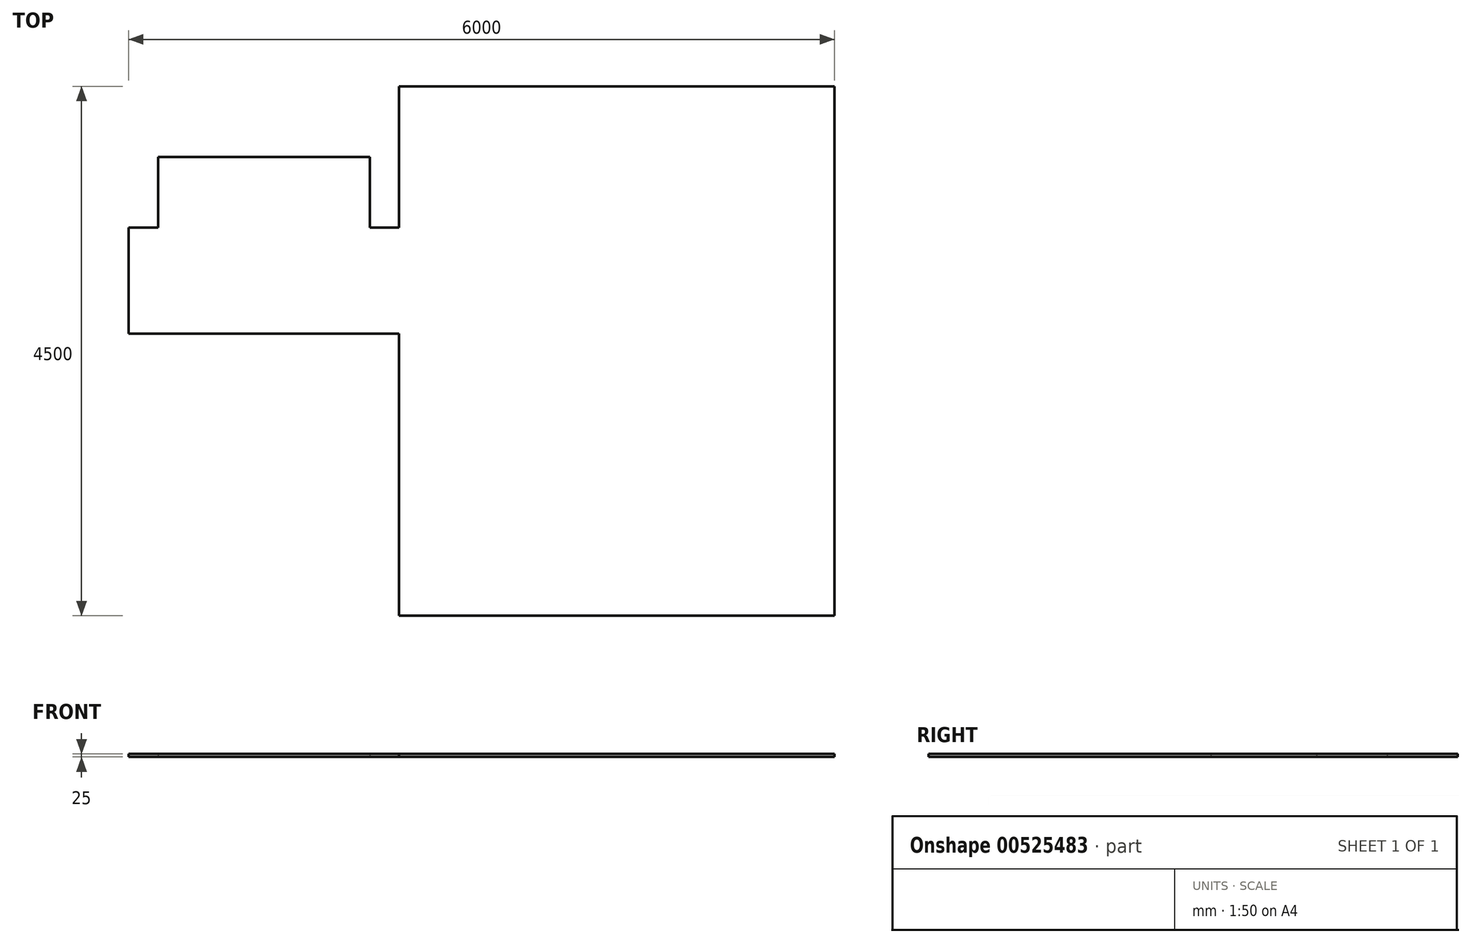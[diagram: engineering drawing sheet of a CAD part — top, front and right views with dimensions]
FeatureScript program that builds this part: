
annotation { "Feature Type Name" : "Feature", "Feature Type Description" : "" }
export const myFeature = defineFeature(function(context is Context, id is Id, definition is map)
    precondition{}
    {
        {
            var Q0;
            Q0=qCreatedBy(makeId("Top.planeOp"),FACE);
            var sketch = newSketch(context, id + "F0", { "sketchPlane" : qUnion([Q0])});
            skLineSegment(sketch, "E0.bottom", {"start": v(0, 0) * mm, "end": v(3700, 0) * mm});
            skLineSegment(sketch, "E0.top", {"start": v(0, 4500) * mm, "end": v(3700, 4500) * mm});
            skLineSegment(sketch, "E0.left", {"start": v(0, 0) * mm, "end": v(0, 2400) * mm});
            skLineSegment(sketch, "E0.right", {"start": v(3700, 0) * mm, "end": v(3700, 4500) * mm});
            skLineSegment(sketch, "E1", {"start": v(0, 3300) * mm, "end": v(-2300, 3300) * mm});
            skLineSegment(sketch, "E2", {"start": v(-2300, 3300) * mm, "end": v(-2300, 2400) * mm});
            skLineSegment(sketch, "E3", {"start": v(-2300, 2400) * mm, "end": v(0, 2400) * mm});
            skLineSegment(sketch, "E4.trimOffspring", {"start": v(0, 3300) * mm, "end": v(0, 4500) * mm});
            skLineSegment(sketch, "E5", {"start": v(-2050, 3300) * mm, "end": v(-2050, 3900) * mm});
            skLineSegment(sketch, "E6", {"start": v(-2050, 3900) * mm, "end": v(-250, 3900) * mm});
            skLineSegment(sketch, "E7", {"start": v(-250, 3900) * mm, "end": v(-250, 3300) * mm});
            skLineSegment(sketch, "E8", {"start": v(-2300, 2500) * mm, "end": v(-1700, 2500) * mm});
            skArc(sketch, "E9", {"start": v(-1700, 2500) * mm, "mid": v(-1875.74, 2924.26) * mm, "end": v(-2300, 3100) * mm});
            skSolve(sketch);
        }
        {
            var Q0;
            Q0=makeQuery(id+"F0.imprint","IMPRINT",FACE,{"disambiguationData":[TD([[makeQuery(id+"F0.imprint","IMPRINT",EDGE,{"derivedFrom":sQuery(id+"F0.wireOp",EDGE,"E0.bottom")}),1.0]])]});
            var Q1;
            {var subQ0=sQuery(id+"F0.wireOp",EDGE,"E8");Q1=makeQuery(id+"F0.imprint","IMPRINT",FACE,{"disambiguationData":[TD([[makeQuery(id+"F0.imprint","IMPRINT",EDGE,{"derivedFrom":subQ0}),1.0]])]});}
            var Q2;
            {var subQ0=sQuery(id+"F0.wireOp",EDGE,"E5");Q2=makeQuery(id+"F0.imprint","IMPRINT",FACE,{"disambiguationData":[TD([[makeQuery(id+"F0.imprint","IMPRINT",EDGE,{"derivedFrom":subQ0}),-1.0]])]});}
            extrude(context, id + "F1", {"entities" : qUnion([Q0, Q1, Q2]), "depth" : 25 * mm, "offsetDistance" : 25 * mm});
        }
    });
